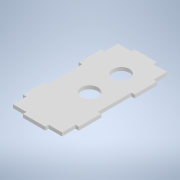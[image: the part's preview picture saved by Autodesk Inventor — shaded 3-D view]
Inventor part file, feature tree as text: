
AUTODESK INVENTOR PART (.ipt)
format: ipt  version: 2020.3 (Build 243373000, 373)  size: 175,104 bytes
history: native  units: mm
features: extrude x3, sketch x3
ambient origin geometry x8: Origin, YZ Plane, XZ Plane, XY Plane, X Axis, Y Axis, Z Axis, Center Point
bodies: Solid1 (feature_tree)
feature tree (6):
  extrude  "Base"  Depth=50.0mm
  extrude  "Tabs"  Depth=15.0mm
  extrude  "Extrusion4"  Depth=20.0mm
  sketch  "Sketch1"  dims[d0=100.0mm d1=50.0mm]
  sketch  "Sketch2"  dims[d2=3.0mm d3=0.0mm d10=15.0mm]
  sketch  "Sketch4"  dims[d11=15.0mm d12=20.0mm d13=20.0mm d14=30.0mm d15=3.0mm d16=0.0mm d17=0.0mm d21=3.0mm d22=10.0mm d31=25.0mm d32=28.397mm d33=25.0mm d34=25.0mm d35=15.0mm d36=15.0mm d37=15.0mm d38=0.0mm d39=20.0mm]
